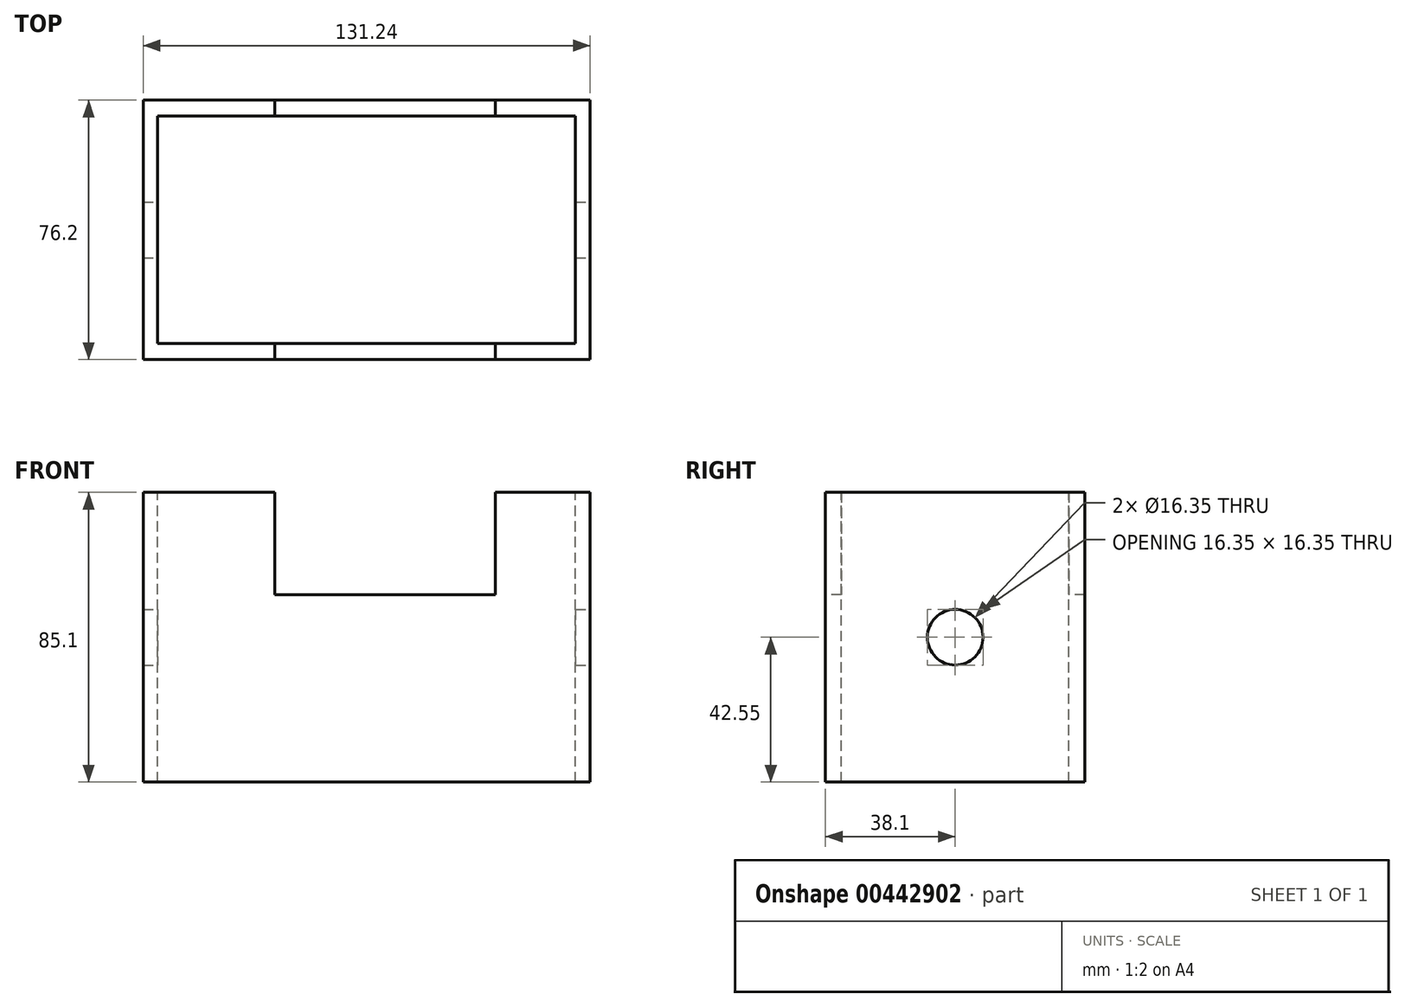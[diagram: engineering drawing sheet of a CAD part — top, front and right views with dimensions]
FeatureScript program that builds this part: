
annotation { "Feature Type Name" : "Feature", "Feature Type Description" : "" }
export const myFeature = defineFeature(function(context is Context, id is Id, definition is map)
    precondition{}
    {
        {
            var Q0;
            Q0=qCreatedBy(makeId("Front.planeOp"),FACE);
            var sketch = newSketch(context, id + "F0", { "sketchPlane" : qUnion([Q0])});
            skLineSegment(sketch, "E0.bottom", {"start": v(-65.62, 42.55) * mm, "end": v(65.62, 42.55) * mm});
            skLineSegment(sketch, "E0.top", {"start": v(-65.62, -42.55) * mm, "end": v(65.62, -42.55) * mm});
            skLineSegment(sketch, "E0.left", {"start": v(-65.62, 42.55) * mm, "end": v(-65.62, -42.55) * mm});
            skLineSegment(sketch, "E0.right", {"start": v(65.62, 42.55) * mm, "end": v(65.62, -42.55) * mm});
            skPoint(sketch, "E0.middle", {"position": v(0, 0) * mm});
            skSolve(sketch);
        }
        {
            var Q0;
            Q0=makeQuery(id+"F0.imprint","IMPRINT",FACE,{"disambiguationData":[TD([[makeQuery(id+"F0.imprint","IMPRINT",EDGE,{"derivedFrom":sQuery(id+"F0.wireOp",EDGE,"E0.bottom")}),-1.0]])]});
            extrude(context, id + "F1", {"entities" : qUnion([Q0]), "depth" : 76.2 * mm, "symmetric" : true});
        }
        {
            var Q0;
            Q0=makeQuery(id+"F1.opExtrude","SWEPT_FACE",FACE,{"disambiguationData":[OSD([sQuery(id+"F0.wireOp",EDGE,"E0.bottom")])]});
            var sketch = newSketch(context, id + "F2", { "sketchPlane" : qUnion([Q0])});
            skLineSegment(sketch, "E1.bottom", {"start": v(-61.32, 33.38) * mm, "end": v(61.32, 33.38) * mm});
            skLineSegment(sketch, "E1.top", {"start": v(-61.32, -33.38) * mm, "end": v(61.32, -33.38) * mm});
            skLineSegment(sketch, "E1.left", {"start": v(-61.32, 33.38) * mm, "end": v(-61.32, -33.38) * mm});
            skLineSegment(sketch, "E1.right", {"start": v(61.32, 33.38) * mm, "end": v(61.32, -33.38) * mm});
            skPoint(sketch, "E1.middle", {"position": v(0, 0) * mm});
            skSolve(sketch);
        }
        {
            var Q0;
            Q0 = qSketchRegion(id + "F2", true);
            extrude(context, id + "F3", {"entities" : qUnion([Q0]), "operationType" : NewBodyOperationType.REMOVE, "oppositeDirection" : true, "depth" : 109.98 * mm});
        }
        {
            var Q0;
            Q0=makeQuery(id+"F1.opExtrude","SWEPT_FACE",FACE,{"disambiguationData":[OSD([sQuery(id+"F0.wireOp",EDGE,"E0.right")])]});
            var sketch = newSketch(context, id + "F4", { "sketchPlane" : qUnion([Q0])});
            skCircle(sketch, "E2", {"center": v(0, 0) * mm, "radius": 8.18 * mm});
            skSolve(sketch);
        }
        {
            var Q0;
            Q0=makeQuery(id+"F4.imprint","IMPRINT",FACE,{"disambiguationData":[TD([[makeQuery(id+"F4.imprint","IMPRINT",EDGE,{"derivedFrom":sQuery(id+"F4.wireOp",EDGE,"E2")}),1.0]])]});
            extrude(context, id + "F5", {"entities" : qUnion([Q0]), "operationType" : NewBodyOperationType.REMOVE, "oppositeDirection" : true, "depth" : 175.5 * mm});
        }
        {
            var Q0;
            Q0=makeQuery(id+"F1.opExtrude","CAP_FACE",FACE,{"disambiguationData":[OSD([sQuery(id+"F0.wireOp",EDGE,"E0.bottom"),sQuery(id+"F0.wireOp",EDGE,"E0.top"),sQuery(id+"F0.wireOp",EDGE,"E0.left"),sQuery(id+"F0.wireOp",EDGE,"E0.right")])],"isStart":false});
            var sketch = newSketch(context, id + "F6", { "sketchPlane" : qUnion([Q0])});
            skLineSegment(sketch, "E3", {"start": v(37.83, 48.86) * mm, "end": v(37.83, 12.47) * mm});
            skLineSegment(sketch, "E4", {"start": v(37.83, 12.47) * mm, "end": v(-26.94, 12.47) * mm});
            skLineSegment(sketch, "E5", {"start": v(-26.94, 12.47) * mm, "end": v(-26.94, 48.86) * mm});
            skLineSegment(sketch, "E6", {"start": v(-26.94, 48.86) * mm, "end": v(37.83, 48.86) * mm});
            skSolve(sketch);
        }
        {
            var Q0;
            Q0 = qSketchRegion(id + "F6", true);
            extrude(context, id + "F7", {"entities" : qUnion([Q0]), "operationType" : NewBodyOperationType.REMOVE, "oppositeDirection" : true, "depth" : 112.78 * mm});
        }
    });
